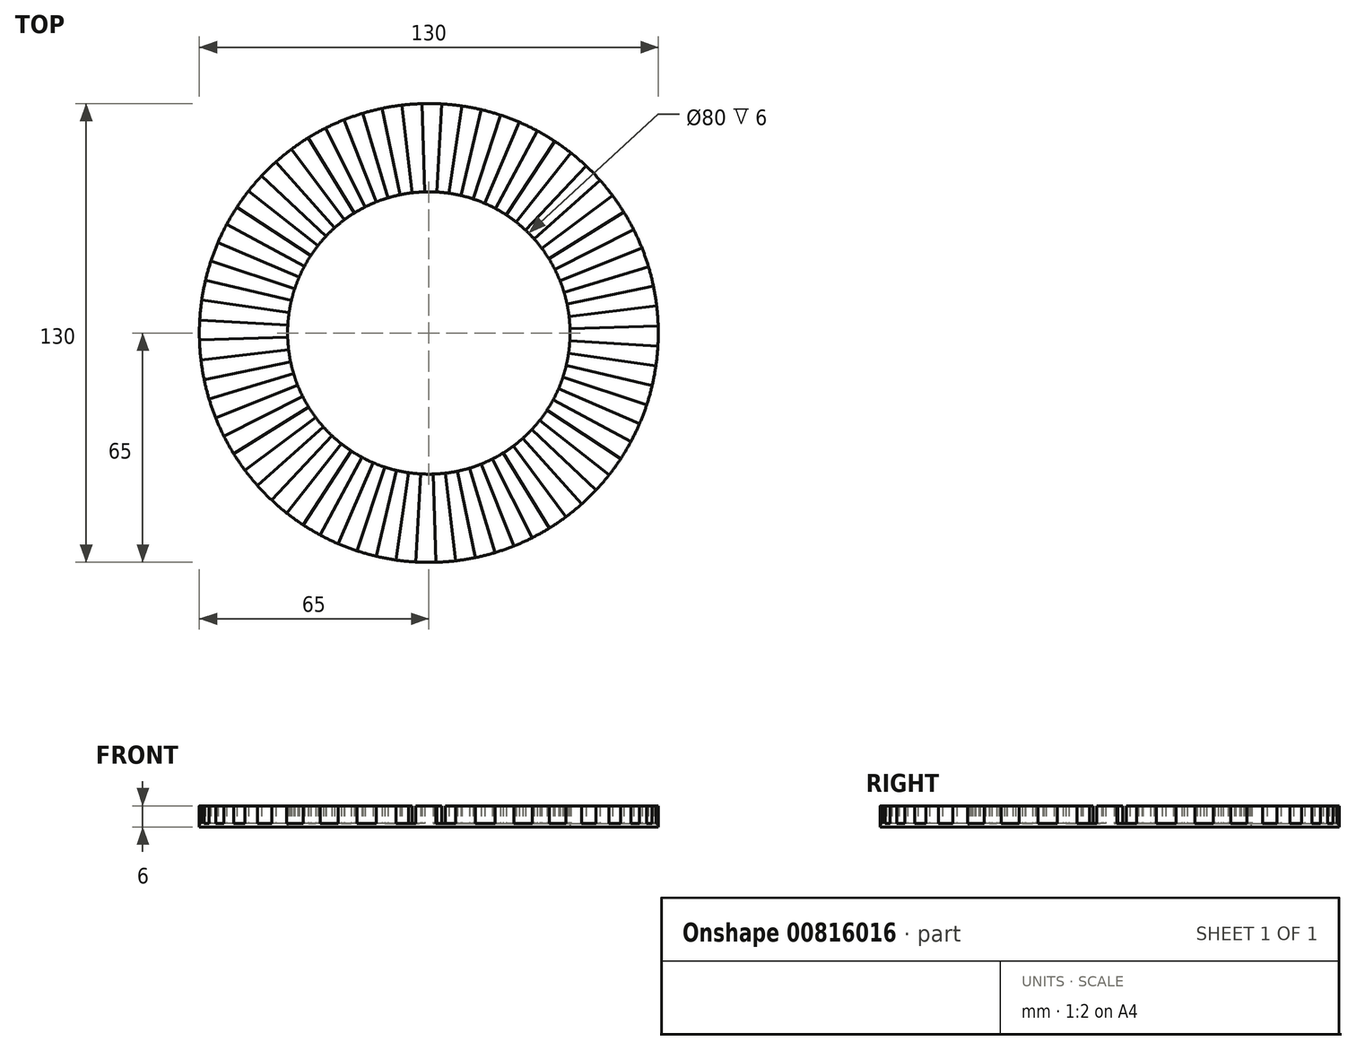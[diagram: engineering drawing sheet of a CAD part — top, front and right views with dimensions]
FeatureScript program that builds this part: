
annotation { "Feature Type Name" : "Feature", "Feature Type Description" : "" }
export const myFeature = defineFeature(function(context is Context, id is Id, definition is map)
    precondition{}
    {
        {
            var Q0;
            Q0=qCreatedBy(makeId("Top.planeOp"),FACE);
            var sketch = newSketch(context, id + "F0", { "sketchPlane" : qUnion([Q0])});
            skCircle(sketch, "E0", {"center": v(0, 0) * mm, "radius": 65 * mm});
            skCircle(sketch, "E1", {"center": v(0, 0) * mm, "radius": 40 * mm});
            skSolve(sketch);
        }
        {
            var Q0;
            Q0=makeQuery(id+"F0.imprint","IMPRINT",FACE,{"disambiguationData":[TD([[makeQuery(id+"F0.imprint","IMPRINT",EDGE,{"derivedFrom":sQuery(id+"F0.wireOp",EDGE,"E0")}),1.0]])]});
            extrude(context, id + "F1", {"entities" : qUnion([Q0]), "depth" : 1 * mm, "offsetDistance" : 25 * mm});
        }
        {
            var Q0;
            Q0=makeQuery(id+"F1.opExtrude","CAP_FACE",FACE,{"disambiguationData":[OSD([sQuery(id+"F0.wireOp",EDGE,"E0"),sQuery(id+"F0.wireOp",EDGE,"E1")])],"isStart":false});
            var sketch = newSketch(context, id + "F2", { "sketchPlane" : qUnion([Q0])});
            skLineSegment(sketch, "E2", {"start": v(36.75, -15.79) * mm, "end": v(59.72, -25.66) * mm});
            skLineSegment(sketch, "E3.1.0", {"start": v(37.99, -12.53) * mm, "end": v(61.73, -20.35) * mm});
            skLineSegment(sketch, "E3.2.0", {"start": v(38.94, -9.17) * mm, "end": v(63.27, -14.9) * mm});
            skPoint(sketch, "E3.center", {"position": v(0, 0) * mm});
            skLineSegment(sketch, "E4.1.3.0", {"start": v(39.59, -5.74) * mm, "end": v(64.33, -9.32) * mm});
            skLineSegment(sketch, "E4.1.4.0", {"start": v(39.94, -2.27) * mm, "end": v(64.9, -3.68) * mm});
            skLineSegment(sketch, "E4.1.5.0", {"start": v(39.98, 1.22) * mm, "end": v(64.97, 1.99) * mm});
            skLineSegment(sketch, "E4.1.6.0", {"start": v(39.72, 4.7) * mm, "end": v(64.55, 7.64) * mm});
            skLineSegment(sketch, "E4.1.7.0", {"start": v(39.16, 8.15) * mm, "end": v(63.64, 13.24) * mm});
            skLineSegment(sketch, "E4.1.8.0", {"start": v(38.3, 11.53) * mm, "end": v(62.24, 18.74) * mm});
            skLineSegment(sketch, "E4.1.9.0", {"start": v(37.15, 14.82) * mm, "end": v(60.37, 24.09) * mm});
            skLineSegment(sketch, "E4.1.10.0", {"start": v(35.72, 18) * mm, "end": v(58.04, 29.26) * mm});
            skLineSegment(sketch, "E4.1.11.0", {"start": v(34.01, 21.05) * mm, "end": v(55.27, 34.2) * mm});
            skLineSegment(sketch, "E4.1.12.0", {"start": v(32.05, 23.93) * mm, "end": v(52.08, 38.9) * mm});
            skLineSegment(sketch, "E4.1.13.0", {"start": v(29.84, 26.64) * mm, "end": v(48.5, 43.28) * mm});
            skLineSegment(sketch, "E4.1.14.0", {"start": v(27.4, 29.14) * mm, "end": v(44.54, 47.35) * mm});
            skLineSegment(sketch, "E4.1.15.0", {"start": v(24.76, 31.41) * mm, "end": v(40.24, 51.05) * mm});
            skLineSegment(sketch, "E4.1.16.0", {"start": v(21.93, 33.45) * mm, "end": v(35.64, 54.36) * mm});
            skLineSegment(sketch, "E4.1.17.0", {"start": v(18.93, 35.24) * mm, "end": v(30.76, 57.26) * mm});
            skLineSegment(sketch, "E4.1.18.0", {"start": v(15.79, 36.75) * mm, "end": v(25.66, 59.72) * mm});
            skLineSegment(sketch, "E4.1.19.0", {"start": v(12.53, 37.99) * mm, "end": v(20.35, 61.73) * mm});
            skLineSegment(sketch, "E4.1.20.0", {"start": v(9.17, 38.94) * mm, "end": v(14.9, 63.27) * mm});
            skLineSegment(sketch, "E4.1.21.0", {"start": v(5.74, 39.59) * mm, "end": v(9.32, 64.33) * mm});
            skLineSegment(sketch, "E4.1.22.0", {"start": v(2.27, 39.94) * mm, "end": v(3.68, 64.9) * mm});
            skLineSegment(sketch, "E4.1.23.0", {"start": v(-1.22, 39.98) * mm, "end": v(-1.99, 64.97) * mm});
            skLineSegment(sketch, "E4.1.24.0", {"start": v(-4.7, 39.72) * mm, "end": v(-7.64, 64.55) * mm});
            skLineSegment(sketch, "E4.1.25.0", {"start": v(-8.15, 39.16) * mm, "end": v(-13.24, 63.64) * mm});
            skLineSegment(sketch, "E4.1.26.0", {"start": v(-11.53, 38.3) * mm, "end": v(-18.74, 62.24) * mm});
            skLineSegment(sketch, "E4.1.27.0", {"start": v(-14.82, 37.15) * mm, "end": v(-24.09, 60.37) * mm});
            skLineSegment(sketch, "E4.1.28.0", {"start": v(-18, 35.72) * mm, "end": v(-29.26, 58.04) * mm});
            skLineSegment(sketch, "E4.1.29.0", {"start": v(-21.05, 34.01) * mm, "end": v(-34.2, 55.27) * mm});
            skLineSegment(sketch, "E4.1.30.0", {"start": v(-23.93, 32.05) * mm, "end": v(-38.9, 52.08) * mm});
            skLineSegment(sketch, "E4.1.31.0", {"start": v(-26.64, 29.84) * mm, "end": v(-43.28, 48.5) * mm});
            skLineSegment(sketch, "E4.1.32.0", {"start": v(-29.14, 27.4) * mm, "end": v(-47.35, 44.54) * mm});
            skLineSegment(sketch, "E4.1.33.0", {"start": v(-31.41, 24.76) * mm, "end": v(-51.05, 40.24) * mm});
            skLineSegment(sketch, "E4.1.34.0", {"start": v(-33.45, 21.93) * mm, "end": v(-54.36, 35.64) * mm});
            skLineSegment(sketch, "E4.1.35.0", {"start": v(-35.24, 18.93) * mm, "end": v(-57.26, 30.76) * mm});
            skLineSegment(sketch, "E5.1.36.0", {"start": v(-36.75, 15.79) * mm, "end": v(-59.72, 25.66) * mm});
            skLineSegment(sketch, "E5.1.37.0", {"start": v(-37.99, 12.53) * mm, "end": v(-61.73, 20.35) * mm});
            skLineSegment(sketch, "E5.1.38.0", {"start": v(-38.94, 9.17) * mm, "end": v(-63.27, 14.9) * mm});
            skLineSegment(sketch, "E5.1.39.0", {"start": v(-39.59, 5.74) * mm, "end": v(-64.33, 9.32) * mm});
            skLineSegment(sketch, "E5.1.40.0", {"start": v(-39.94, 2.27) * mm, "end": v(-64.9, 3.68) * mm});
            skLineSegment(sketch, "E5.1.41.0", {"start": v(-39.98, -1.22) * mm, "end": v(-64.97, -1.99) * mm});
            skLineSegment(sketch, "E5.1.42.0", {"start": v(-39.72, -4.7) * mm, "end": v(-64.55, -7.64) * mm});
            skLineSegment(sketch, "E5.1.43.0", {"start": v(-39.16, -8.15) * mm, "end": v(-63.64, -13.24) * mm});
            skLineSegment(sketch, "E5.1.44.0", {"start": v(-38.3, -11.53) * mm, "end": v(-62.24, -18.74) * mm});
            skLineSegment(sketch, "E5.1.45.0", {"start": v(-37.15, -14.82) * mm, "end": v(-60.37, -24.09) * mm});
            skLineSegment(sketch, "E5.1.46.0", {"start": v(-35.72, -18) * mm, "end": v(-58.04, -29.26) * mm});
            skLineSegment(sketch, "E5.1.47.0", {"start": v(-34.01, -21.05) * mm, "end": v(-55.27, -34.2) * mm});
            skLineSegment(sketch, "E5.1.48.0", {"start": v(-32.05, -23.93) * mm, "end": v(-52.08, -38.9) * mm});
            skLineSegment(sketch, "E5.1.49.0", {"start": v(-29.84, -26.64) * mm, "end": v(-48.5, -43.28) * mm});
            skLineSegment(sketch, "E5.1.50.0", {"start": v(-27.4, -29.14) * mm, "end": v(-44.54, -47.35) * mm});
            skLineSegment(sketch, "E5.1.51.0", {"start": v(-24.76, -31.41) * mm, "end": v(-40.24, -51.05) * mm});
            skLineSegment(sketch, "E5.1.52.0", {"start": v(-21.93, -33.45) * mm, "end": v(-35.64, -54.36) * mm});
            skLineSegment(sketch, "E5.1.53.0", {"start": v(-18.93, -35.24) * mm, "end": v(-30.76, -57.26) * mm});
            skLineSegment(sketch, "E5.1.54.0", {"start": v(-15.79, -36.75) * mm, "end": v(-25.66, -59.72) * mm});
            skLineSegment(sketch, "E5.1.55.0", {"start": v(-12.53, -37.99) * mm, "end": v(-20.35, -61.73) * mm});
            skLineSegment(sketch, "E5.1.56.0", {"start": v(-9.17, -38.94) * mm, "end": v(-14.9, -63.27) * mm});
            skLineSegment(sketch, "E5.1.57.0", {"start": v(-5.74, -39.59) * mm, "end": v(-9.32, -64.33) * mm});
            skLineSegment(sketch, "E5.1.58.0", {"start": v(-2.27, -39.94) * mm, "end": v(-3.68, -64.9) * mm});
            skLineSegment(sketch, "E5.1.59.0", {"start": v(1.22, -39.98) * mm, "end": v(1.99, -64.97) * mm});
            skLineSegment(sketch, "E5.1.60.0", {"start": v(4.7, -39.72) * mm, "end": v(7.64, -64.55) * mm});
            skLineSegment(sketch, "E5.1.61.0", {"start": v(8.15, -39.16) * mm, "end": v(13.24, -63.64) * mm});
            skLineSegment(sketch, "E5.1.62.0", {"start": v(11.53, -38.3) * mm, "end": v(18.74, -62.24) * mm});
            skLineSegment(sketch, "E5.1.63.0", {"start": v(14.82, -37.15) * mm, "end": v(24.09, -60.37) * mm});
            skLineSegment(sketch, "E5.1.64.0", {"start": v(18, -35.72) * mm, "end": v(29.26, -58.04) * mm});
            skLineSegment(sketch, "E5.1.65.0", {"start": v(21.05, -34.01) * mm, "end": v(34.2, -55.27) * mm});
            skLineSegment(sketch, "E5.1.66.0", {"start": v(23.93, -32.05) * mm, "end": v(38.9, -52.08) * mm});
            skLineSegment(sketch, "E5.1.67.0", {"start": v(26.64, -29.84) * mm, "end": v(43.28, -48.5) * mm});
            skLineSegment(sketch, "E5.1.68.0", {"start": v(29.14, -27.4) * mm, "end": v(47.35, -44.54) * mm});
            skLineSegment(sketch, "E5.1.69.0", {"start": v(31.41, -24.76) * mm, "end": v(51.05, -40.24) * mm});
            skLineSegment(sketch, "E5.1.70.0", {"start": v(33.45, -21.93) * mm, "end": v(54.36, -35.64) * mm});
            skLineSegment(sketch, "E5.1.71.0", {"start": v(35.24, -18.93) * mm, "end": v(57.26, -30.76) * mm});
            skSolve(sketch);
        }
        {
            var Q0;
            {var subQ0=sQuery(id+"F2.wireOp",EDGE,"E5.1.52.0");Q0=makeQuery(id+"F2.imprint","IMPRINT",FACE,{"disambiguationData":[TD([[makeQuery(id+"F2.imprint","IMPRINT",EDGE,{"derivedFrom":subQ0}),1.0]])]});}
            var Q1;
            {var subQ0=sQuery(id+"F2.wireOp",EDGE,"E5.1.54.0");Q1=makeQuery(id+"F2.imprint","IMPRINT",FACE,{"disambiguationData":[TD([[makeQuery(id+"F2.imprint","IMPRINT",EDGE,{"derivedFrom":subQ0}),1.0]])]});}
            var Q2;
            {var subQ0=sQuery(id+"F2.wireOp",EDGE,"E5.1.56.0");Q2=makeQuery(id+"F2.imprint","IMPRINT",FACE,{"disambiguationData":[TD([[makeQuery(id+"F2.imprint","IMPRINT",EDGE,{"derivedFrom":subQ0}),1.0]])]});}
            var Q3;
            {var subQ0=sQuery(id+"F2.wireOp",EDGE,"E5.1.58.0");Q3=makeQuery(id+"F2.imprint","IMPRINT",FACE,{"disambiguationData":[TD([[makeQuery(id+"F2.imprint","IMPRINT",EDGE,{"derivedFrom":subQ0}),1.0]])]});}
            var Q4;
            {var subQ0=sQuery(id+"F2.wireOp",EDGE,"E5.1.60.0");Q4=makeQuery(id+"F2.imprint","IMPRINT",FACE,{"disambiguationData":[TD([[makeQuery(id+"F2.imprint","IMPRINT",EDGE,{"derivedFrom":subQ0}),1.0]])]});}
            var Q5;
            {var subQ0=sQuery(id+"F2.wireOp",EDGE,"E5.1.62.0");Q5=makeQuery(id+"F2.imprint","IMPRINT",FACE,{"disambiguationData":[TD([[makeQuery(id+"F2.imprint","IMPRINT",EDGE,{"derivedFrom":subQ0}),1.0]])]});}
            var Q6;
            {var subQ0=sQuery(id+"F2.wireOp",EDGE,"E5.1.64.0");Q6=makeQuery(id+"F2.imprint","IMPRINT",FACE,{"disambiguationData":[TD([[makeQuery(id+"F2.imprint","IMPRINT",EDGE,{"derivedFrom":subQ0}),1.0]])]});}
            var Q7;
            {var subQ0=sQuery(id+"F2.wireOp",EDGE,"E5.1.66.0");Q7=makeQuery(id+"F2.imprint","IMPRINT",FACE,{"disambiguationData":[TD([[makeQuery(id+"F2.imprint","IMPRINT",EDGE,{"derivedFrom":subQ0}),1.0]])]});}
            var Q8;
            {var subQ0=sQuery(id+"F2.wireOp",EDGE,"E5.1.68.0");Q8=makeQuery(id+"F2.imprint","IMPRINT",FACE,{"disambiguationData":[TD([[makeQuery(id+"F2.imprint","IMPRINT",EDGE,{"derivedFrom":subQ0}),1.0]])]});}
            var Q9;
            {var subQ0=sQuery(id+"F2.wireOp",EDGE,"E5.1.70.0");Q9=makeQuery(id+"F2.imprint","IMPRINT",FACE,{"disambiguationData":[TD([[makeQuery(id+"F2.imprint","IMPRINT",EDGE,{"derivedFrom":subQ0}),1.0]])]});}
            var Q10;
            {var subQ0=sQuery(id+"F2.wireOp",EDGE,"E2");Q10=makeQuery(id+"F2.imprint","IMPRINT",FACE,{"disambiguationData":[TD([[makeQuery(id+"F2.imprint","IMPRINT",EDGE,{"derivedFrom":subQ0}),1.0]])]});}
            var Q11;
            {var subQ0=sQuery(id+"F2.wireOp",EDGE,"E3.2.0");Q11=makeQuery(id+"F2.imprint","IMPRINT",FACE,{"disambiguationData":[TD([[makeQuery(id+"F2.imprint","IMPRINT",EDGE,{"derivedFrom":subQ0}),1.0]])]});}
            var Q12;
            {var subQ0=sQuery(id+"F2.wireOp",EDGE,"E4.1.4.0");Q12=makeQuery(id+"F2.imprint","IMPRINT",FACE,{"disambiguationData":[TD([[makeQuery(id+"F2.imprint","IMPRINT",EDGE,{"derivedFrom":subQ0}),1.0]])]});}
            var Q13;
            {var subQ0=sQuery(id+"F2.wireOp",EDGE,"E4.1.6.0");Q13=makeQuery(id+"F2.imprint","IMPRINT",FACE,{"disambiguationData":[TD([[makeQuery(id+"F2.imprint","IMPRINT",EDGE,{"derivedFrom":subQ0}),1.0]])]});}
            var Q14;
            {var subQ0=sQuery(id+"F2.wireOp",EDGE,"E4.1.8.0");Q14=makeQuery(id+"F2.imprint","IMPRINT",FACE,{"disambiguationData":[TD([[makeQuery(id+"F2.imprint","IMPRINT",EDGE,{"derivedFrom":subQ0}),1.0]])]});}
            var Q15;
            {var subQ0=sQuery(id+"F2.wireOp",EDGE,"E4.1.10.0");Q15=makeQuery(id+"F2.imprint","IMPRINT",FACE,{"disambiguationData":[TD([[makeQuery(id+"F2.imprint","IMPRINT",EDGE,{"derivedFrom":subQ0}),1.0]])]});}
            var Q16;
            {var subQ0=sQuery(id+"F2.wireOp",EDGE,"E4.1.12.0");Q16=makeQuery(id+"F2.imprint","IMPRINT",FACE,{"disambiguationData":[TD([[makeQuery(id+"F2.imprint","IMPRINT",EDGE,{"derivedFrom":subQ0}),1.0]])]});}
            var Q17;
            {var subQ0=sQuery(id+"F2.wireOp",EDGE,"E4.1.14.0");Q17=makeQuery(id+"F2.imprint","IMPRINT",FACE,{"disambiguationData":[TD([[makeQuery(id+"F2.imprint","IMPRINT",EDGE,{"derivedFrom":subQ0}),1.0]])]});}
            var Q18;
            {var subQ0=sQuery(id+"F2.wireOp",EDGE,"E4.1.16.0");Q18=makeQuery(id+"F2.imprint","IMPRINT",FACE,{"disambiguationData":[TD([[makeQuery(id+"F2.imprint","IMPRINT",EDGE,{"derivedFrom":subQ0}),1.0]])]});}
            var Q19;
            {var subQ0=sQuery(id+"F2.wireOp",EDGE,"E4.1.18.0");Q19=makeQuery(id+"F2.imprint","IMPRINT",FACE,{"disambiguationData":[TD([[makeQuery(id+"F2.imprint","IMPRINT",EDGE,{"derivedFrom":subQ0}),1.0]])]});}
            var Q20;
            {var subQ0=sQuery(id+"F2.wireOp",EDGE,"E4.1.20.0");Q20=makeQuery(id+"F2.imprint","IMPRINT",FACE,{"disambiguationData":[TD([[makeQuery(id+"F2.imprint","IMPRINT",EDGE,{"derivedFrom":subQ0}),1.0]])]});}
            var Q21;
            {var subQ0=sQuery(id+"F2.wireOp",EDGE,"E4.1.22.0");Q21=makeQuery(id+"F2.imprint","IMPRINT",FACE,{"disambiguationData":[TD([[makeQuery(id+"F2.imprint","IMPRINT",EDGE,{"derivedFrom":subQ0}),1.0]])]});}
            var Q22;
            {var subQ0=sQuery(id+"F2.wireOp",EDGE,"E4.1.24.0");Q22=makeQuery(id+"F2.imprint","IMPRINT",FACE,{"disambiguationData":[TD([[makeQuery(id+"F2.imprint","IMPRINT",EDGE,{"derivedFrom":subQ0}),1.0]])]});}
            var Q23;
            {var subQ0=sQuery(id+"F2.wireOp",EDGE,"E4.1.26.0");Q23=makeQuery(id+"F2.imprint","IMPRINT",FACE,{"disambiguationData":[TD([[makeQuery(id+"F2.imprint","IMPRINT",EDGE,{"derivedFrom":subQ0}),1.0]])]});}
            var Q24;
            {var subQ0=sQuery(id+"F2.wireOp",EDGE,"E4.1.28.0");Q24=makeQuery(id+"F2.imprint","IMPRINT",FACE,{"disambiguationData":[TD([[makeQuery(id+"F2.imprint","IMPRINT",EDGE,{"derivedFrom":subQ0}),1.0]])]});}
            var Q25;
            {var subQ0=sQuery(id+"F2.wireOp",EDGE,"E4.1.30.0");Q25=makeQuery(id+"F2.imprint","IMPRINT",FACE,{"disambiguationData":[TD([[makeQuery(id+"F2.imprint","IMPRINT",EDGE,{"derivedFrom":subQ0}),1.0]])]});}
            var Q26;
            {var subQ0=sQuery(id+"F2.wireOp",EDGE,"E4.1.32.0");Q26=makeQuery(id+"F2.imprint","IMPRINT",FACE,{"disambiguationData":[TD([[makeQuery(id+"F2.imprint","IMPRINT",EDGE,{"derivedFrom":subQ0}),1.0]])]});}
            var Q27;
            {var subQ0=sQuery(id+"F2.wireOp",EDGE,"E4.1.34.0");Q27=makeQuery(id+"F2.imprint","IMPRINT",FACE,{"disambiguationData":[TD([[makeQuery(id+"F2.imprint","IMPRINT",EDGE,{"derivedFrom":subQ0}),1.0]])]});}
            var Q28;
            {var subQ0=sQuery(id+"F2.wireOp",EDGE,"E5.1.36.0");Q28=makeQuery(id+"F2.imprint","IMPRINT",FACE,{"disambiguationData":[TD([[makeQuery(id+"F2.imprint","IMPRINT",EDGE,{"derivedFrom":subQ0}),1.0]])]});}
            var Q29;
            {var subQ0=sQuery(id+"F2.wireOp",EDGE,"E5.1.38.0");Q29=makeQuery(id+"F2.imprint","IMPRINT",FACE,{"disambiguationData":[TD([[makeQuery(id+"F2.imprint","IMPRINT",EDGE,{"derivedFrom":subQ0}),1.0]])]});}
            var Q30;
            {var subQ0=sQuery(id+"F2.wireOp",EDGE,"E5.1.40.0");Q30=makeQuery(id+"F2.imprint","IMPRINT",FACE,{"disambiguationData":[TD([[makeQuery(id+"F2.imprint","IMPRINT",EDGE,{"derivedFrom":subQ0}),1.0]])]});}
            var Q31;
            {var subQ0=sQuery(id+"F2.wireOp",EDGE,"E5.1.42.0");Q31=makeQuery(id+"F2.imprint","IMPRINT",FACE,{"disambiguationData":[TD([[makeQuery(id+"F2.imprint","IMPRINT",EDGE,{"derivedFrom":subQ0}),1.0]])]});}
            var Q32;
            {var subQ0=sQuery(id+"F2.wireOp",EDGE,"E5.1.44.0");Q32=makeQuery(id+"F2.imprint","IMPRINT",FACE,{"disambiguationData":[TD([[makeQuery(id+"F2.imprint","IMPRINT",EDGE,{"derivedFrom":subQ0}),1.0]])]});}
            var Q33;
            {var subQ0=sQuery(id+"F2.wireOp",EDGE,"E5.1.46.0");Q33=makeQuery(id+"F2.imprint","IMPRINT",FACE,{"disambiguationData":[TD([[makeQuery(id+"F2.imprint","IMPRINT",EDGE,{"derivedFrom":subQ0}),1.0]])]});}
            var Q34;
            {var subQ0=sQuery(id+"F2.wireOp",EDGE,"E5.1.48.0");Q34=makeQuery(id+"F2.imprint","IMPRINT",FACE,{"disambiguationData":[TD([[makeQuery(id+"F2.imprint","IMPRINT",EDGE,{"derivedFrom":subQ0}),1.0]])]});}
            var Q35;
            {var subQ0=sQuery(id+"F2.wireOp",EDGE,"E5.1.50.0");Q35=makeQuery(id+"F2.imprint","IMPRINT",FACE,{"disambiguationData":[TD([[makeQuery(id+"F2.imprint","IMPRINT",EDGE,{"derivedFrom":subQ0}),1.0]])]});}
            extrude(context, id + "F3", {"entities" : qUnion([Q0, Q1, Q2, Q3, Q4, Q5, Q6, Q7, Q8, Q9, Q10, Q11, Q12, Q13, Q14, Q15, Q16, Q17, Q18, Q19, Q20, Q21, Q22, Q23, Q24, Q25, Q26, Q27, Q28, Q29, Q30, Q31, Q32, Q33, Q34, Q35]), "operationType" : NewBodyOperationType.ADD, "depth" : 5 * mm, "offsetDistance" : 25 * mm});
        }
    });
